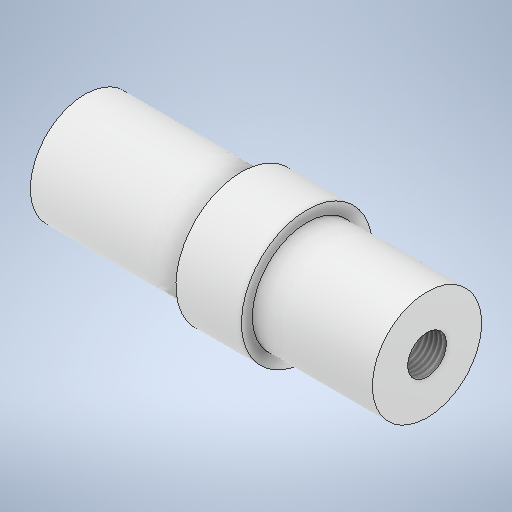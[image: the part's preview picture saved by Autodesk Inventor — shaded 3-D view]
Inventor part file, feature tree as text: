
AUTODESK INVENTOR PART (.ipt)
format: ipt  version: 2025.2 (Build 292293000, 293)  size: 283,648 bytes
history: native  units: in
note: dims shown in document units (in); Inventor stores cm internally (conversion verified against a paired STEP export)
features: other x3, plane x2, hole x2, sketch x2
ambient origin geometry x8: Origin, YZ Plane, XZ Plane, XY Plane, X Axis, Y Axis, Z Axis, Center Point
bodies: Volumenkörper1 (feature_tree)
feature tree (9):
  other  "Skelett_Laufkatze.ipt"
  other  "Welle_Kettenzug"
  plane  "Arbeitsebene1"
  hole  "Bohrung1"  [1 undecoded]
  plane  "Arbeitsebene2"
  hole  "Bohrung2"  [1 undecoded]
  other  "Kettenzug_welle"
  sketch  "Skizze2"  dims[d0=0.3937in d1=90.0deg]
  sketch  "Skizze3"  dims[d2=0.0in d3=0.4192in d4=0.9449in d5=0.1575in d6=0.0787in d7=90.0deg d8=1.189in d9=0.8108in d10=0.0in d11=0.4192in d12=0.9449in d13=0.1575in d14=0.0787in d15=90.0deg d16=1.189in d17=0.8108in]
note: 2 required parameter values undecoded (feature->parameter linkage not recoverable at this tier; creation-order binding heuristic only, values carry confidence <= 0.55)
